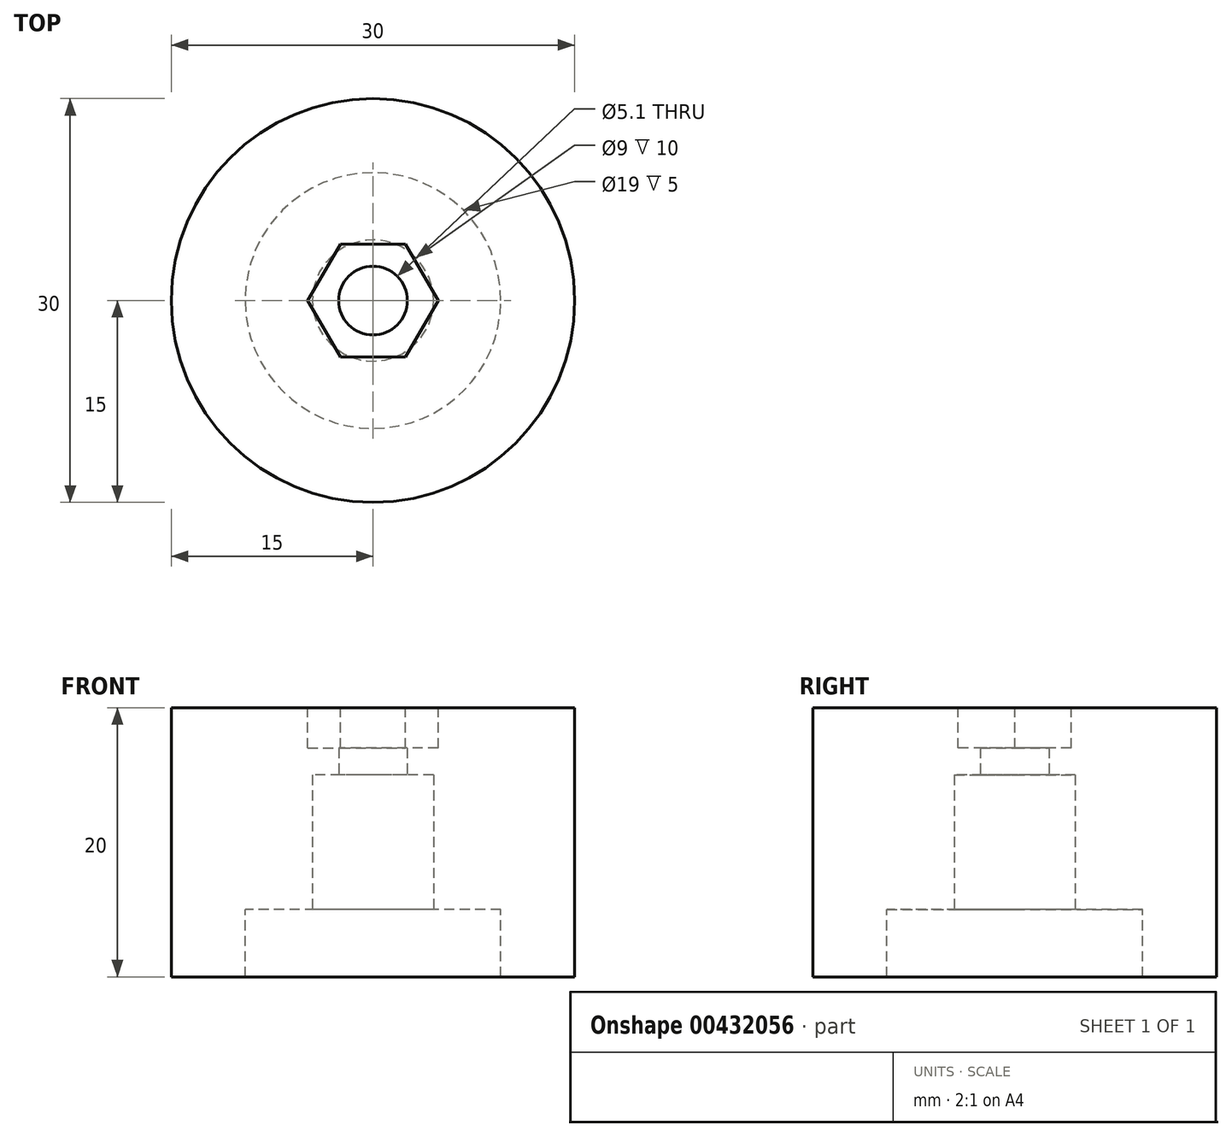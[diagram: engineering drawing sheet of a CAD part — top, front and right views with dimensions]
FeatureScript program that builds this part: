
annotation { "Feature Type Name" : "Feature", "Feature Type Description" : "" }
export const myFeature = defineFeature(function(context is Context, id is Id, definition is map)
    precondition{}
    {
        {
            var Q0;
            Q0=qCreatedBy(makeId("Top.planeOp"),FACE);
            var sketch = newSketch(context, id + "F0", { "sketchPlane" : qUnion([Q0])});
            skCircle(sketch, "E0", {"center": v(0, 0) * mm, "radius": 15 * mm});
            skCircle(sketch, "E1", {"center": v(0, 0) * mm, "radius": 9.5 * mm});
            skCircle(sketch, "E2", {"center": v(0, 0) * mm, "radius": 2.55 * mm});
            skCircle(sketch, "E3", {"center": v(0, 0) * mm, "radius": 4.5 * mm});
            skSolve(sketch);
        }
        {
            var Q0;
            Q0=makeQuery(id+"F0.imprint","IMPRINT",FACE,{"disambiguationData":[TD([[makeQuery(id+"F0.imprint","IMPRINT",EDGE,{"derivedFrom":sQuery(id+"F0.wireOp",EDGE,"E1")}),1.0]])]});
            var Q1;
            Q1=makeQuery(id+"F0.imprint","IMPRINT",FACE,{"disambiguationData":[TD([[makeQuery(id+"F0.imprint","IMPRINT",EDGE,{"derivedFrom":sQuery(id+"F0.wireOp",EDGE,"E0")}),1.0]])]});
            var Q2;
            Q2=makeQuery(id+"F0.imprint","IMPRINT",FACE,{"disambiguationData":[TD([[makeQuery(id+"F0.imprint","IMPRINT",EDGE,{"derivedFrom":sQuery(id+"F0.wireOp",EDGE,"E2")}),-1.0]])]});
            extrude(context, id + "F1", {"entities" : qUnion([Q0, Q1, Q2]), "depth" : 15 * mm});
        }
        {
            var Q0;
            Q0=makeQuery(id+"F1.opExtrude","CAP_FACE",FACE,{"disambiguationData":[OSD([sQuery(id+"F0.wireOp",EDGE,"E0")])],"isStart":false});
            var sketch = newSketch(context, id + "F2", { "sketchPlane" : qUnion([Q0])});
            skCircle(sketch, "E4.cCircle", {"center": v(0, 0) * mm, "radius": 4.2 * mm, "construction": true});
            skLineSegment(sketch, "E4.0", {"start": v(4.85, 0) * mm, "end": v(2.42, -4.2) * mm});
            skLineSegment(sketch, "E4.1", {"start": v(2.42, -4.2) * mm, "end": v(-2.42, -4.2) * mm});
            skLineSegment(sketch, "E4.2", {"start": v(-2.42, -4.2) * mm, "end": v(-4.85, 0) * mm});
            skLineSegment(sketch, "E4.3", {"start": v(-4.85, 0) * mm, "end": v(-2.42, 4.2) * mm});
            skLineSegment(sketch, "E4.4", {"start": v(-2.42, 4.2) * mm, "end": v(2.42, 4.2) * mm});
            skLineSegment(sketch, "E4.5", {"start": v(2.42, 4.2) * mm, "end": v(4.85, 0) * mm});
            skPoint(sketch, "E4.0.midPoint", {"position": v(3.64, -2.1) * mm});
            skSolve(sketch);
        }
        {
            var Q0;
            Q0=qSketchRegion(id+"F2",true);
            extrude(context, id + "F3", {"entities" : qUnion([Q0]), "operationType" : NewBodyOperationType.REMOVE, "oppositeDirection" : true, "depth" : 3 * mm});
        }
        {
            var Q0;
            Q0=makeQuery(id+"F0.imprint","IMPRINT",FACE,{"disambiguationData":[TD([[makeQuery(id+"F0.imprint","IMPRINT",EDGE,{"derivedFrom":sQuery(id+"F0.wireOp",EDGE,"E2")}),-1.0]])]});
            extrude(context, id + "F4", {"entities" : qUnion([Q0]), "operationType" : NewBodyOperationType.REMOVE, "depth" : 10 * mm});
        }
        {
            var Q0;
            Q0=makeQuery(id+"F0.imprint","IMPRINT",FACE,{"disambiguationData":[TD([[makeQuery(id+"F0.imprint","IMPRINT",EDGE,{"derivedFrom":sQuery(id+"F0.wireOp",EDGE,"E0")}),1.0]])]});
            extrude(context, id + "F5", {"entities" : qUnion([Q0]), "operationType" : NewBodyOperationType.ADD, "oppositeDirection" : true, "depth" : 5 * mm});
        }
    });
